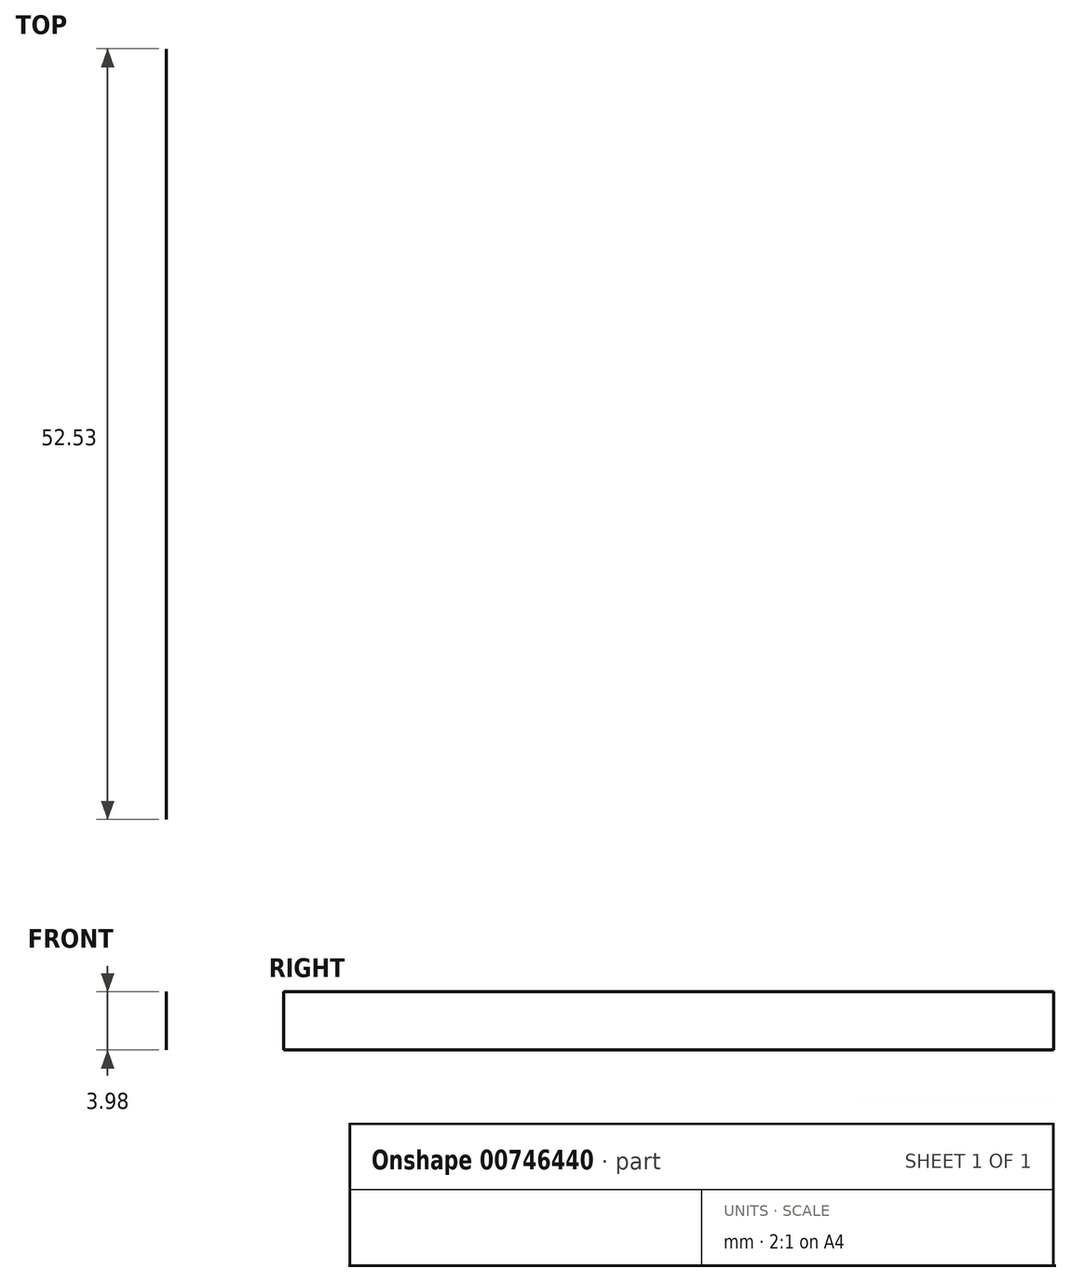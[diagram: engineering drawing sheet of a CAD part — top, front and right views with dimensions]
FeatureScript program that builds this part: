
annotation { "Feature Type Name" : "Feature", "Feature Type Description" : "" }
export const myFeature = defineFeature(function(context is Context, id is Id, definition is map)
    precondition{}
    {
        {
            var Q0;
            Q0=qCreatedBy(makeId("Top.planeOp"),FACE);
            var sketch = newSketch(context, id + "F0", { "sketchPlane" : qUnion([Q0])});
            skLineSegment(sketch, "E0", {"start": v(47.41, 0) * mm, "end": v(0, 52.53) * mm});
            skLineSegment(sketch, "E1", {"start": v(0, 52.53) * mm, "end": v(0, 0) * mm});
            skLineSegment(sketch, "E2", {"start": v(0, 0) * mm, "end": v(47.41, 0) * mm});
            skSolve(sketch);
        }
        {
            var Q0;
            Q0=sQuery(id+"F0.wireOp",EDGE,"E1");
            extrude(context, id + "F1", {"bodyType" : ToolBodyType.SURFACE, "surfaceEntities" : qUnion([Q0]), "depth" : 3.98 * mm, "offsetDistance" : 25.4 * mm});
        }
    });
